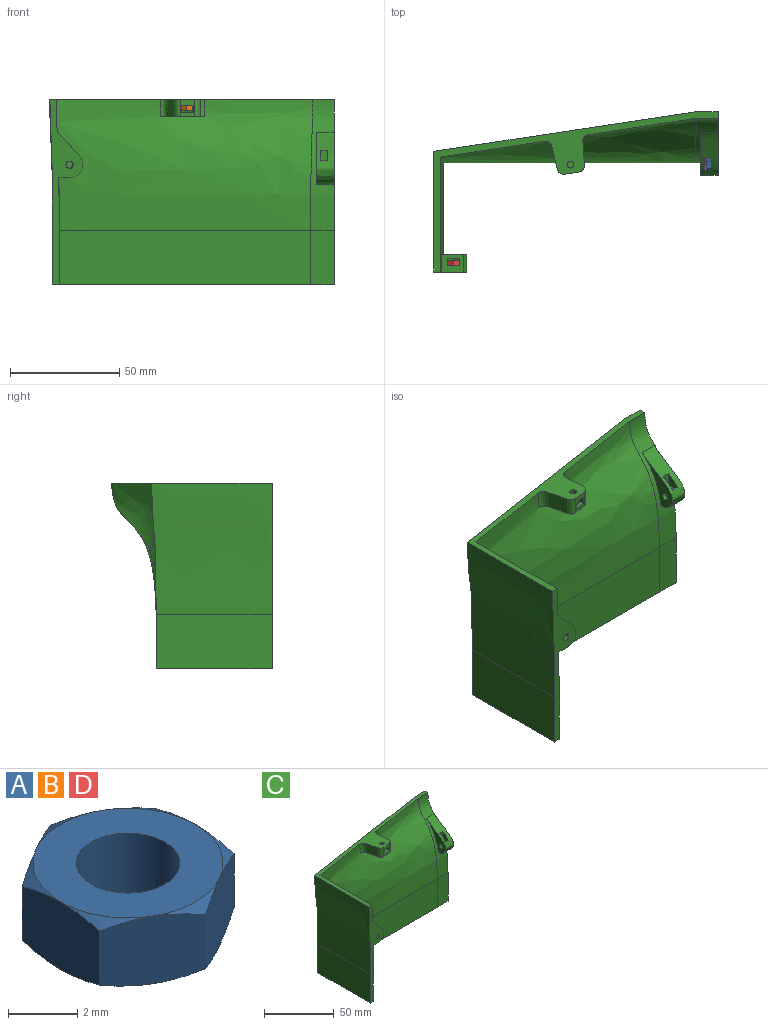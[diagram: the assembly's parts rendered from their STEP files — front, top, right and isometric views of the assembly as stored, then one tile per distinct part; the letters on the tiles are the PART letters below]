
ASSEMBLY  parts=4 mates=3
PART A: 21 faces, bbox 6.6x6.6x2.7 mm
  f0: plane 5.5x5.5mm, normal (0,0,1), area 16.7mm2, adj f2,f3,f4,f7,f9,f11,f13
  f1: plane 5.5x5.5mm, normal (0,0,-1), area 16.7mm2, adj f2,f5,f6,f8,f10,f12,f14
  f2: cylinder r=1.5mm len=3mm, axis (0,0,-1), area 22.6mm2, adj f0,f1
  f3: cone r=3.18mm half-angle=60deg, axis (0,0,-1), area 0.7mm2, adj f0,f15,f20
  f4: cone r=3.18mm half-angle=60deg, axis (0,0,-1), area 0.7mm2, adj f0,f15,f16
  f5: cone r=3.18mm half-angle=60deg, axis (0,0,1), area 0.7mm2, adj f1,f15,f20
  f6: cone r=3.18mm half-angle=60deg, axis (0,0,1), area 0.7mm2, adj f1,f15,f16
  f7: cone r=3.18mm half-angle=60deg, axis (0,0,-1), area 0.7mm2, adj f0,f16,f17
  f8: cone r=3.18mm half-angle=60deg, axis (0,0,1), area 0.7mm2, adj f1,f16,f17
  f9: cone r=3.18mm half-angle=60deg, axis (0,0,-1), area 0.7mm2, adj f0,f17,f18
  f10: cone r=3.18mm half-angle=60deg, axis (0,0,1), area 0.7mm2, adj f1,f17,f18
  f11: cone r=3.18mm half-angle=60deg, axis (0,0,-1), area 0.7mm2, adj f0,f18,f19
  f12: cone r=3.18mm half-angle=60deg, axis (0,0,1), area 0.7mm2, adj f1,f18,f19
  f13: cone r=3.18mm half-angle=60deg, axis (0,0,-1), area 0.7mm2, adj f0,f19,f20
  f14: cone r=3.18mm half-angle=60deg, axis (0,0,1), area 0.7mm2, adj f1,f19,f20
  f15: plane 3.01x2.67mm, normal (0.5,-0.87,0), area 7.1mm2, adj f3,f4,f5,f6,f16,f20
  f16: plane 3.01x2.67mm, normal (-0.5,-0.87,0), area 7.1mm2, adj f4,f6,f7,f8,f15,f17
  f17: plane 3.44x2.66mm, normal (-1,0,0), area 7.1mm2, adj f7,f8,f9,f10,f16,f18
  f18: plane 3.01x2.67mm, normal (-0.5,0.87,0), area 7.1mm2, adj f9,f10,f11,f12,f17,f19
  f19: plane 3.01x2.67mm, normal (0.5,0.87,0), area 7.1mm2, adj f11,f12,f13,f14,f18,f20
  f20: plane 3.44x2.66mm, normal (1,0,0), area 7.1mm2, adj f3,f5,f13,f14,f15,f19
PART B: same geometry as A
PART C: 57 faces, bbox 136.4x79.9x92.1 mm
  f0: cylinder r=1.6mm len=3.2mm, axis (0,0,1), area 16.1mm2, adj f25,f52
  f1: cylinder r=1.65mm len=3.3mm, axis (0,-1,0), area 18.7mm2, adj f35,f39
  f2: plane 11.18x10.15mm, normal (0.74,0,0.67), area 93.2mm2, adj f7,f34,f35,f37,f39,f40,f41,f42
  f3: offset ~65.9x61.17mm, area 2883.7mm2, adj f7,f8,f13,f34,f35,f36,f48
  f4: extruded ~23.97x19.56mm, area 277.4mm2, adj f6,f15,f16,f17,f18,f19,f20
  f5: cylinder r=1.6mm len=3.2mm, axis (1,0,0), area 18.1mm2, adj f15,f19
  f6: offset ~65.9x26.32mm, area 458.6mm2, adj f4,f8,f9,f13,f15,f16,f46
  f7: plane 88.42x18.55mm, normal (0,-1,0), area 399.8mm2, adj f2,f3,f8,f12,f36,f37,f38,f48
  f8: plane 130.12x73.41mm, normal (0,0,1), area 762mm2, adj f3,f6,f7,f9,f10,f11,f12,f13
  f9: bspline ~59.9x37.99mm, area 196.3mm2, adj f6,f8,f10,f45
  f10: bspline ~59.9x20.33mm, area 682.4mm2, adj f8,f9,f11,f50
  f11: bspline ~120.11x59.9mm, area 7392.8mm2, adj f8,f10,f12,f50
  f12: bspline ~59.9x55.17mm, area 3224.2mm2, adj f7,f8,f11,f49
  f13: offset ~127.31x65.9mm, area 7049.8mm2, adj f3,f6,f8,f25,f47,f53,f54
  f14: cylinder r=1.6mm len=3.2mm, axis (1,0,0), area 30.2mm2, adj f16,f20
  f15: plane 30.01x26.2mm, normal (-1,0,0), area 119.9mm2, adj f4,f5,f6
  f16: plane 30.01x26.2mm, normal (1,0,0), area 119.9mm2, adj f4,f6,f14
  f17: plane 10.81x3.2mm, normal (0,-1,0), area 34.6mm2, adj f4,f19,f20,f22
  f18: plane 6.17x3.2mm, normal (0,1,0), area 19.8mm2, adj f4,f19,f20,f21
  f19: plane 12.56x5.96mm, normal (1,0,0), area 47.1mm2, adj f4,f5,f17,f18,f21,f22
  f20: plane 12.56x5.96mm, normal (-1,0,0), area 47.1mm2, adj f4,f14,f17,f18,f21,f22
  f21: plane 3.2x2.9mm, normal (0,0.5,0.87), area 10.7mm2, adj f18,f19,f20,f22
  f22: plane 3.2x2.9mm, normal (0,-0.5,0.87), area 10.7mm2, adj f17,f19,f20,f21
  f23: plane 10.56x8mm, normal (-0.97,-0.24,0), area 85.5mm2, adj f8,f25,f53,f56
  f24: plane 10.84x8.01mm, normal (1,0.06,0), area 85mm2, adj f8,f25,f54,f55
  f25: plane 20.37x17.76mm, normal (0,0,-1), area 201.6mm2, adj f0,f13,f23,f24,f26,f53,f54,f55
  f26: plane 8x6.43mm, normal (0.15,-0.99,0), area 33.5mm2, adj f8,f25,f28,f29,f32,f33,f55,f56
  f27: cylinder r=1.6mm len=3.2mm, axis (0,0,1), area 30.2mm2, adj f8,f33
  f28: plane 5.61x3.2mm, normal (0.99,0.15,0), area 18.2mm2, adj f26,f31,f32,f33
  f29: plane 5.61x3.2mm, normal (-0.99,-0.15,0), area 18.2mm2, adj f26,f30,f32,f33
  f30: plane 3.2x3.12mm, normal (-0.36,-0.93,0), area 10.7mm2, adj f29,f31,f32,f33
  f31: plane 3.2x2.62mm, normal (0.62,-0.78,0), area 10.7mm2, adj f28,f30,f32,f33
  f32: plane 7.7x6.58mm, normal (0,0,1), area 37.8mm2, adj f26,f28,f29,f30,f31
  f33: plane 7.7x6.58mm, normal (0,0,-1), area 29.7mm2, adj f26,f27,f28,f29,f30,f31
  f34: plane 8x0.01mm, normal (-1,0,-0.04), area 0.1mm2, adj f2,f3,f35
  f35: plane 27.6x18.1mm, normal (0,1,0), area 145.1mm2, adj f1,f2,f3,f34,f36,f37
  f36: plane 8x4.88mm, normal (0,0,-1), area 39mm2, adj f3,f7,f35,f37
  f37: cylinder r=6mm len=10.03mm, axis (0,-1,0), area 110.8mm2, adj f2,f7,f35,f36
  f38: cylinder r=1.65mm len=3.3mm, axis (0,-1,0), area 31.1mm2, adj f7,f40
  f39: plane 15.47x5.8mm, normal (0,-1,0), area 57.8mm2, adj f1,f2,f41,f42,f43,f44
  f40: plane 15.47x5.8mm, normal (0,1,0), area 57.8mm2, adj f2,f38,f41,f42,f43,f44
  f41: plane 7.41x3.2mm, normal (-1,0,0), area 23.7mm2, adj f2,f39,f40,f44
  f42: plane 13.8x3.2mm, normal (1,0,0), area 44.1mm2, adj f2,f39,f40,f43
  f43: plane 3.2x2.9mm, normal (0.5,0,0.87), area 10.7mm2, adj f39,f40,f42,f44
  f44: plane 3.2x2.9mm, normal (-0.5,0,0.87), area 10.7mm2, adj f39,f40,f41,f43
  f45: plane 25x3mm, normal (1,0,0), area 75mm2, adj f9,f46,f50,f51
  f46: plane 25x10.74mm, normal (0,-1,0), area 268.6mm2, adj f6,f45,f47,f51
  f47: plane 115x25mm, normal (0,-1,0), area 2875mm2, adj f13,f46,f48,f51
  f48: plane 50x25mm, normal (1,0,0), area 1250mm2, adj f3,f7,f47,f51
  f49: plane 53x25mm, normal (-1,0,0), area 1325mm2, adj f7,f12,f50,f51
  f50: plane 128.74x25mm, normal (0,1,0), area 3218.6mm2, adj f10,f11,f45,f49,f51
  f51: plane 128.74x53mm, normal (0,0,-1), area 536.2mm2, adj f7,f45,f46,f47,f48,f49,f50
  f52: plane 3.2x3.2mm, normal (0,0,-1), area 8mm2, adj f0
  f53: bspline ~10.27x3.54mm, area 36mm2, adj f8,f13,f23,f25
  f54: bspline ~9.46x4.03mm, area 36.4mm2, adj f8,f13,f24,f25
  f55: cylinder r=3mm len=8mm, axis (0,0,-1), area 35.6mm2, adj f8,f24,f25,f26
  f56: cylinder r=3mm len=8mm, axis (0,0,-1), area 35.6mm2, adj f8,f23,f25,f26
PART D: same geometry as A
PLACE A rot(axis=(-0.71,0,-0.71),180deg) t=(-150.94,-2.02,-60.67)mm
PLACE B t=(-223.04,-2.03,-23.57)mm
PLACE C t=(-271.28,-1.02,-78.07)mm fixed
PLACE D rot(axis=(1,0,0),90deg) t=(-276.51,-45.77,-48.17)mm
MATE fastened A.f2 <-> C.f5  axis (-1,0,0) through (-148.54,-2.02,-50.67)mm
MATE fastened D.f2 <-> C.f1  axis (0,1,0) through (-266.51,-48.17,-48.17)mm
MATE fastened B.f2 <-> C.f0  axis (0,0,1) through (-213.04,-2.03,-21.17)mm
